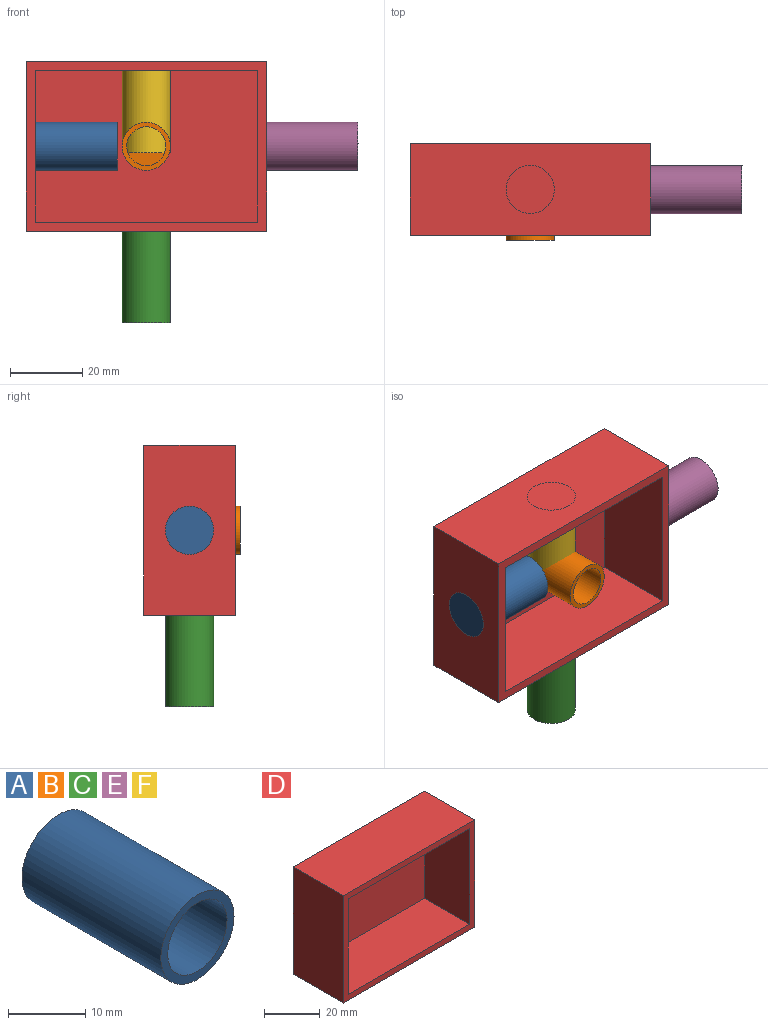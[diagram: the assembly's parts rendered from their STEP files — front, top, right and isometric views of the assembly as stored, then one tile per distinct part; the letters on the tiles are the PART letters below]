
ASSEMBLY  parts=6 mates=5
PART A: 5 faces, bbox 13.4x25.4x13.4 mm
  f0: cylinder r=6.69mm len=25.4mm, axis (0,1,0), area 1067.2mm2, adj f1,f2
  f1: plane 13.37x13.37mm, normal (0,-1,0), area 48.3mm2, adj f0,f3
  f2: plane 13.37x13.37mm, normal (0,1,0), area 140.5mm2, adj f0
  f3: cylinder r=5.42mm len=24.13mm, axis (0,1,0), area 821.3mm2, adj f1,f4
  f4: plane 10.83x10.83mm, normal (0,-1,0), area 92.2mm2, adj f3
PART B: same geometry as A
PART C: same geometry as A
PART D: 11 faces, bbox 66.8x25.4x47.2 mm
  f0: plane 47.18x25.4mm, normal (1,0,0), area 1198.3mm2, adj f1,f3,f4,f5
  f1: plane 66.78x25.4mm, normal (0,0,1), area 1696.2mm2, adj f0,f2,f4,f5
  f2: plane 47.18x25.4mm, normal (-1,0,0), area 1198.3mm2, adj f1,f3,f4,f5
  f3: plane 66.78x25.4mm, normal (0,0,-1), area 1696.2mm2, adj f0,f2,f4,f5
  f4: plane 66.78x47.18mm, normal (0,-1,0), area 553.1mm2, adj f0,f1,f2,f3,f6,f7,f8,f9
  f5: plane 66.78x47.18mm, normal (0,1,0), area 3150.5mm2, adj f0,f1,f2,f3
  f6: plane 42.1x22.86mm, normal (-1,0,0), area 962.3mm2, adj f4,f7,f9,f10
  f7: plane 61.7x22.86mm, normal (0,0,-1), area 1410.5mm2, adj f4,f6,f8,f10
  f8: plane 42.1x22.86mm, normal (1,0,0), area 962.3mm2, adj f4,f7,f9,f10
  f9: plane 61.7x22.86mm, normal (0,0,1), area 1410.5mm2, adj f4,f6,f8,f10
  f10: plane 61.7x42.1mm, normal (0,-1,0), area 2597.4mm2, adj f6,f7,f8,f9
PART E: same geometry as A
PART F: same geometry as A
PLACE A rot(axis=(0,0,1),90deg) t=(-60.15,53.17,-56.68)mm
PLACE B t=(28.76,8.99,-56.68)mm
PLACE C rot(axis=(1,0,0),90deg) t=(28.76,57.16,-20.76)mm
PLACE D t=(-26.76,10.35,2.83)mm
PLACE E rot(axis=(0,0,1),90deg) t=(6.63,53.17,-56.68)mm
PLACE F rot(axis=(1,0,0),90deg) t=(28.76,57.16,26.41)mm
MATE slider B.f0 <-> D.f10  axis (0,1,0) through (-26.76,8.99,2.83)mm
MATE slider A.f0 <-> D.f2  axis (-1,0,0) through (-60.15,-2.35,2.83)mm
MATE slider C.f0 <-> D.f3  axis (0,0,1) through (-26.76,-2.35,-20.76)mm
MATE slider E.f0 <-> D.f0  axis (-1,0,0) through (6.63,-2.35,2.83)mm
MATE slider F.f0 <-> D.f1  axis (0,0,1) through (-26.76,-2.35,26.41)mm
